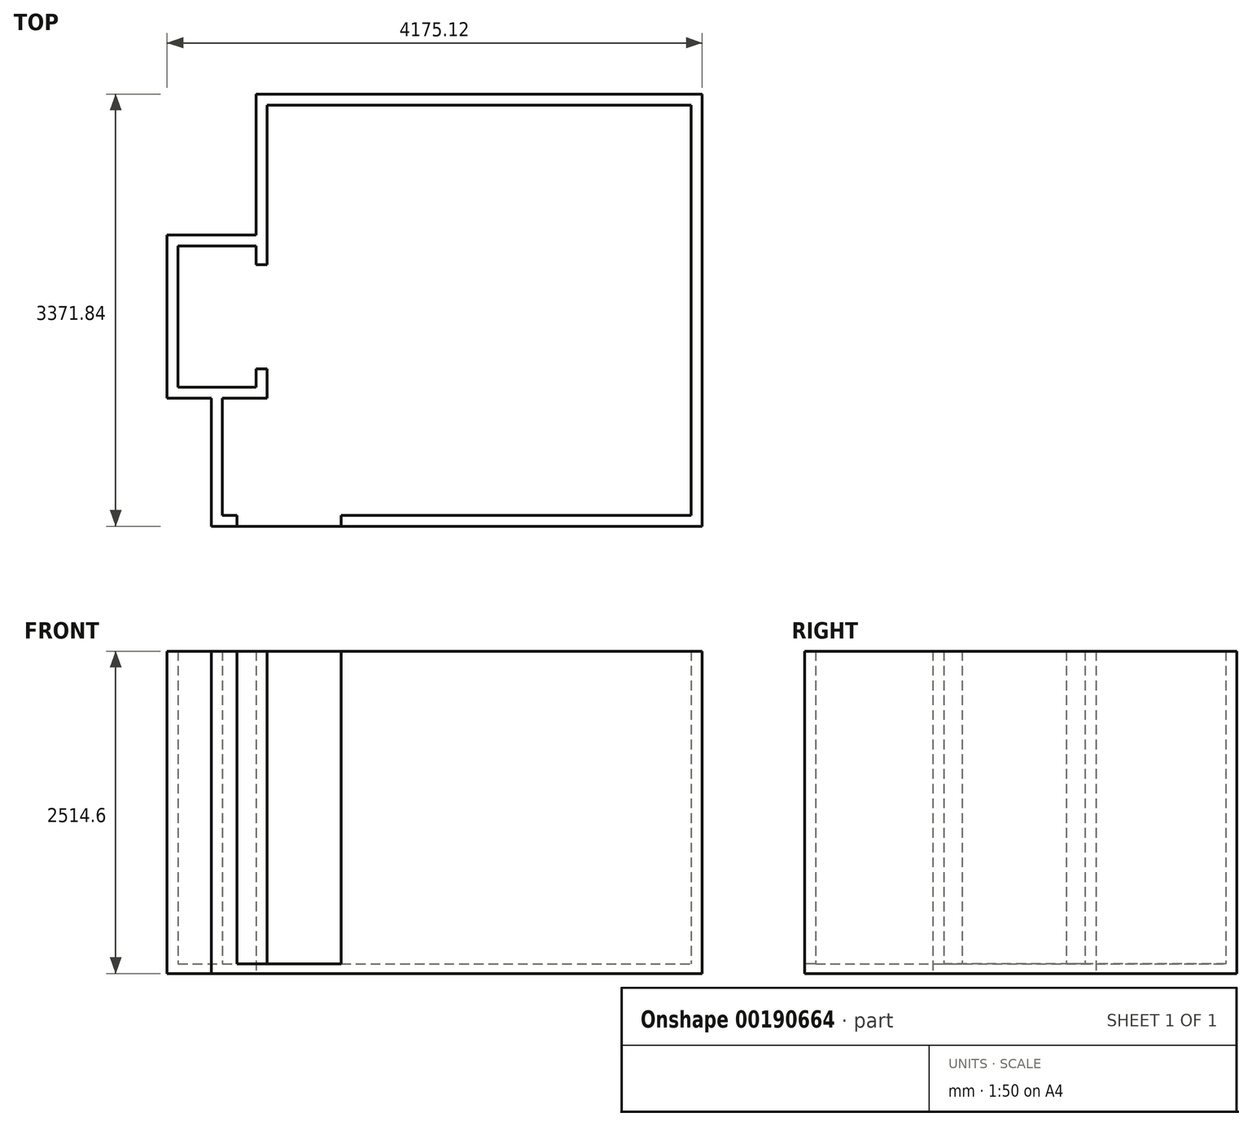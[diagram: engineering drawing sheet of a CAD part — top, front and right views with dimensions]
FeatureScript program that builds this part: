
annotation { "Feature Type Name" : "Feature", "Feature Type Description" : "" }
export const myFeature = defineFeature(function(context is Context, id is Id, definition is map)
    precondition{}
    {
        {
            var Q0;
            Q0=qCreatedBy(makeId("Top.planeOp"),FACE);
            var sketch = newSketch(context, id + "F0", { "sketchPlane" : qUnion([Q0])});
            skLineSegment(sketch, "E0.bottom", {"start": v(0, 0) * mm, "end": v(114.3, 0) * mm});
            skLineSegment(sketch, "E0.top", {"start": v(349.25, 3200.4) * mm, "end": v(3657.6, 3200.4) * mm});
            skLineSegment(sketch, "E0.left", {"start": v(0, 0) * mm, "end": v(0, 914.4) * mm});
            skLineSegment(sketch, "E0.right", {"start": v(3657.6, 0) * mm, "end": v(3657.6, 3200.4) * mm});
            skLineSegment(sketch, "E1.bottom", {"start": v(0, 914.4) * mm, "end": v(349.25, 914.4) * mm});
            skLineSegment(sketch, "E1.right", {"start": v(349.25, 914.4) * mm, "end": v(349.25, 1143) * mm});
            skLineSegment(sketch, "E2", {"start": v(-85.73, -85.73) * mm, "end": v(-85.73, 914.4) * mm});
            skLineSegment(sketch, "E3", {"start": v(-85.73, 1000.13) * mm, "end": v(263.53, 1000.13) * mm});
            skLineSegment(sketch, "E4", {"start": v(263.52, 1000.13) * mm, "end": v(263.52, 1143) * mm});
            skLineSegment(sketch, "E5", {"start": v(263.53, 3286.12) * mm, "end": v(3743.33, 3286.12) * mm});
            skLineSegment(sketch, "E6", {"start": v(3743.33, 3286.12) * mm, "end": v(3743.33, -85.72) * mm});
            skLineSegment(sketch, "E7", {"start": v(3743.33, -85.72) * mm, "end": v(927.1, -85.73) * mm});
            skLineSegment(sketch, "E8.left", {"start": v(114.3, 0) * mm, "end": v(114.3, -85.73) * mm});
            skLineSegment(sketch, "E8.right", {"start": v(927.1, 0) * mm, "end": v(927.1, -85.73) * mm});
            skLineSegment(sketch, "E9.trimOffspring", {"start": v(927.1, 0) * mm, "end": v(3657.6, 0) * mm});
            skLineSegment(sketch, "E10.trimOffspring", {"start": v(114.3, -85.73) * mm, "end": v(-85.73, -85.73) * mm});
            skLineSegment(sketch, "E11.bottom", {"start": v(1066.8, 0) * mm, "end": v(2743.2, 0) * mm});
            skLineSegment(sketch, "E11.top", {"start": v(1066.8, 2133.6) * mm, "end": v(2743.2, 2133.6) * mm});
            skLineSegment(sketch, "E11.left", {"start": v(1066.8, 0) * mm, "end": v(1066.8, 2133.6) * mm});
            skLineSegment(sketch, "E11.right", {"start": v(2743.2, 0) * mm, "end": v(2743.2, 2133.6) * mm});
            skLineSegment(sketch, "E12.bottom", {"start": v(2797.45, 0) * mm, "end": v(3203.85, 0) * mm});
            skLineSegment(sketch, "E12.top", {"start": v(2797.45, 406.4) * mm, "end": v(3203.85, 406.4) * mm});
            skLineSegment(sketch, "E12.left", {"start": v(2797.45, 0) * mm, "end": v(2797.45, 406.4) * mm});
            skLineSegment(sketch, "E12.right", {"start": v(3203.85, 0) * mm, "end": v(3203.85, 406.4) * mm});
            skLineSegment(sketch, "E13.bottom", {"start": v(349.25, 3200.4) * mm, "end": v(1219.2, 3200.4) * mm});
            skLineSegment(sketch, "E13.top", {"start": v(349.25, 2743.2) * mm, "end": v(1219.2, 2743.2) * mm});
            skLineSegment(sketch, "E13.left", {"start": v(349.25, 3200.4) * mm, "end": v(349.25, 2743.2) * mm});
            skLineSegment(sketch, "E13.right", {"start": v(1219.2, 3200.4) * mm, "end": v(1219.2, 2743.2) * mm});
            skLineSegment(sketch, "E14.bottom", {"start": v(3342.64, 637.54) * mm, "end": v(3342.64, 2098.04) * mm});
            skLineSegment(sketch, "E14.top", {"start": v(3647.44, 637.54) * mm, "end": v(3647.44, 2098.04) * mm});
            skLineSegment(sketch, "E14.left", {"start": v(3342.64, 637.54) * mm, "end": v(3647.44, 637.54) * mm});
            skLineSegment(sketch, "E14.right", {"start": v(3342.64, 2098.04) * mm, "end": v(3647.44, 2098.04) * mm});
            skLineSegment(sketch, "E15.bottom", {"start": v(3639.82, 2273.3) * mm, "end": v(3639.82, 3187.7) * mm});
            skLineSegment(sketch, "E15.top", {"start": v(2979.42, 2273.3) * mm, "end": v(2979.42, 3187.7) * mm});
            skLineSegment(sketch, "E15.left", {"start": v(3639.82, 2273.3) * mm, "end": v(2979.42, 2273.3) * mm});
            skLineSegment(sketch, "E15.right", {"start": v(3639.82, 3187.7) * mm, "end": v(2979.42, 3187.7) * mm});
            skLineSegment(sketch, "E16.trimOffspring", {"start": v(349.25, 2641.6) * mm, "end": v(349.25, 3200.4) * mm});
            skLineSegment(sketch, "E17.trimOffspring", {"start": v(263.52, 2629.45) * mm, "end": v(263.52, 3286.13) * mm});
            skLineSegment(sketch, "E18", {"start": v(263.52, 2629.45) * mm, "end": v(263.52, 2185.67) * mm});
            skLineSegment(sketch, "E19", {"start": v(349.25, 2641.6) * mm, "end": v(349.25, 1955.8) * mm});
            skLineSegment(sketch, "E20.bottom", {"start": v(349.25, 1143) * mm, "end": v(263.53, 1143) * mm});
            skLineSegment(sketch, "E20.top", {"start": v(349.25, 1955.8) * mm, "end": v(263.52, 1955.8) * mm});
            skLineSegment(sketch, "E21.bottom", {"start": v(263.53, 2099.95) * mm, "end": v(-346.08, 2099.95) * mm});
            skLineSegment(sketch, "E21.top", {"start": v(263.53, 1000.13) * mm, "end": v(-346.08, 1000.13) * mm});
            skLineSegment(sketch, "E21.left", {"start": v(263.53, 2099.95) * mm, "end": v(263.53, 1955.8) * mm});
            skLineSegment(sketch, "E21.right", {"start": v(-346.08, 2099.95) * mm, "end": v(-346.08, 1000.13) * mm});
            skLineSegment(sketch, "E22", {"start": v(263.52, 1143) * mm, "end": v(263.52, 1000.13) * mm});
            skLineSegment(sketch, "E23.trimOffspring", {"start": v(263.53, 1143) * mm, "end": v(263.53, 1000.13) * mm});
            skLineSegment(sketch, "E24", {"start": v(263.52, 2185.67) * mm, "end": v(-431.8, 2185.67) * mm});
            skLineSegment(sketch, "E25", {"start": v(-431.8, 2185.67) * mm, "end": v(-431.8, 914.4) * mm});
            skLineSegment(sketch, "E26", {"start": v(-431.8, 914.4) * mm, "end": v(-85.72, 914.4) * mm});
            skSolve(sketch);
        }
        {
            var Q0;
            Q0=makeQuery(id+"F0.imprint","IMPRINT",FACE,{"disambiguationData":[TD([[makeQuery(id+"F0.imprint","IMPRINT",EDGE,{"derivedFrom":sQuery(id+"F0.wireOp",EDGE,"E0.bottom")}),-1.0]])]});
            extrude(context, id + "F1", {"entities" : qUnion([Q0]), "depth" : 2438.4 * mm});
        }
        {
            var Q0;
            Q0=makeQuery(id+"F1.opExtrude","CAP_FACE",FACE,{"disambiguationData":[OSD([sQuery(id+"F0.wireOp",EDGE,"E0.bottom"),sQuery(id+"F0.wireOp",EDGE,"E0.top"),sQuery(id+"F0.wireOp",EDGE,"E0.left"),sQuery(id+"F0.wireOp",EDGE,"E0.right"),sQuery(id+"F0.wireOp",EDGE,"E1.bottom"),sQuery(id+"F0.wireOp",EDGE,"E1.right"),sQuery(id+"F0.wireOp",EDGE,"E2"),sQuery(id+"F0.wireOp",EDGE,"E5"),sQuery(id+"F0.wireOp",EDGE,"E6"),sQuery(id+"F0.wireOp",EDGE,"E7"),sQuery(id+"F0.wireOp",EDGE,"E8.left"),sQuery(id+"F0.wireOp",EDGE,"E8.right"),sQuery(id+"F0.wireOp",EDGE,"E9.trimOffspring"),sQuery(id+"F0.wireOp",EDGE,"E10.trimOffspring"),sQuery(id+"F0.wireOp",EDGE,"E11.bottom"),sQuery(id+"F0.wireOp",EDGE,"E12.bottom"),sQuery(id+"F0.wireOp",EDGE,"E13.bottom"),sQuery(id+"F0.wireOp",EDGE,"E14.bottom"),sQuery(id+"F0.wireOp",EDGE,"E15.bottom"),sQuery(id+"F0.wireOp",EDGE,"E15.left"),sQuery(id+"F0.wireOp",EDGE,"E16.trimOffspring"),sQuery(id+"F0.wireOp",EDGE,"E17.trimOffspring"),sQuery(id+"F0.wireOp",EDGE,"E18"),sQuery(id+"F0.wireOp",EDGE,"E19"),sQuery(id+"F0.wireOp",EDGE,"E20.bottom"),sQuery(id+"F0.wireOp",EDGE,"E20.top"),sQuery(id+"F0.wireOp",EDGE,"E21.bottom"),sQuery(id+"F0.wireOp",EDGE,"E21.top"),sQuery(id+"F0.wireOp",EDGE,"E21.right"),sQuery(id+"F0.wireOp",EDGE,"E23.trimOffspring"),sQuery(id+"F0.wireOp",EDGE,"E24"),sQuery(id+"F0.wireOp",EDGE,"E25"),sQuery(id+"F0.wireOp",EDGE,"E26"),sQuery(id+"F0.wireOp",EDGE,"E21.left")])],"isStart":true});
            var sketch = newSketch(context, id + "F2", { "sketchPlane" : qUnion([Q0])});
            skLineSegment(sketch, "E27", {"start": v(-85.73, 85.73) * mm, "end": v(3743.33, 85.72) * mm});
            skLineSegment(sketch, "E28", {"start": v(3743.33, 85.72) * mm, "end": v(3743.33, -3286.12) * mm});
            skLineSegment(sketch, "E29", {"start": v(3743.33, -3286.12) * mm, "end": v(263.52, -3286.12) * mm});
            skLineSegment(sketch, "E30", {"start": v(263.52, -3286.12) * mm, "end": v(263.52, -2185.67) * mm});
            skLineSegment(sketch, "E31", {"start": v(263.52, -2185.67) * mm, "end": v(-431.8, -2185.67) * mm});
            skLineSegment(sketch, "E32", {"start": v(-431.8, -2185.67) * mm, "end": v(-431.8, -914.4) * mm});
            skLineSegment(sketch, "E33", {"start": v(-431.8, -914.4) * mm, "end": v(-85.72, -914.4) * mm});
            skLineSegment(sketch, "E34", {"start": v(-85.72, -914.4) * mm, "end": v(-85.73, 85.73) * mm});
            skSolve(sketch);
        }
        {
            var Q0;
            Q0 = qSketchRegion(id + "F2", true);
            extrude(context, id + "F3", {"entities" : qUnion([Q0]), "operationType" : NewBodyOperationType.ADD, "depth" : 76.2 * mm});
        }
    });
